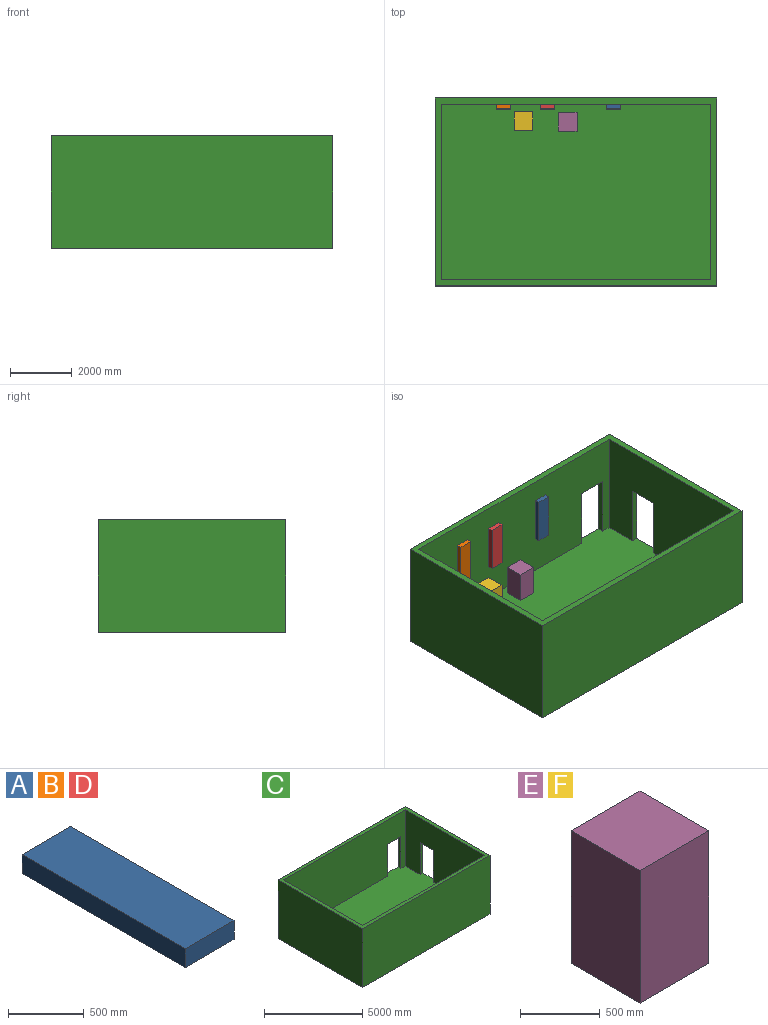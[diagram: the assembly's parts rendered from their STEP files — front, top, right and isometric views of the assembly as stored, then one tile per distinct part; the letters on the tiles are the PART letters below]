
ASSEMBLY  parts=6 mates=5
PART A: 6 faces, bbox 457.2x1524x152.4 mm
  f0: plane 457.2x152.4mm, normal (0,1,0), area 69677.3mm2, adj f1,f3,f4,f5
  f1: plane 1524x152.4mm, normal (-1,0,0), area 232257.6mm2, adj f0,f2,f4,f5
  f2: plane 457.2x152.4mm, normal (0,-1,0), area 69677.3mm2, adj f1,f3,f4,f5
  f3: plane 1524x152.4mm, normal (1,0,0), area 232257.6mm2, adj f0,f2,f4,f5
  f4: plane 1524x457.2mm, normal (0,0,1), area 696772.8mm2, adj f0,f1,f2,f3
  f5: plane 1524x457.2mm, normal (0,0,-1), area 696772.8mm2, adj f0,f1,f2,f3
PART B: same geometry as A
PART C: 17 faces, bbox 9144x6096x3657.6 mm
  f0: plane 1981.2x203.2mm, normal (0,1,0), area 402579.8mm2, adj f4,f5,f10,f16
  f1: plane 1981.2x203.2mm, normal (0,-1,0), area 402579.8mm2, adj f4,f5,f10,f16
  f2: plane 1981.2x203.2mm, normal (1,0,0), area 402579.8mm2, adj f4,f6,f13,f15
  f3: plane 1981.2x203.2mm, normal (-1,0,0), area 402579.8mm2, adj f4,f6,f13,f15
  f4: plane 8940.8x5892.8mm, normal (0,0,1), area 50105706.2mm2, adj f0,f1,f2,f3,f5,f6,f10,f11
  f5: plane 6096x3657.6mm, normal (1,0,0), area 20384475.4mm2, adj f0,f1,f4,f6,f8,f9,f14,f16
  f6: plane 9144x3657.6mm, normal (0,1,0), area 31532840.2mm2, adj f2,f3,f4,f5,f7,f9,f14,f15
  f7: plane 6096x3657.6mm, normal (-1,0,0), area 22296729.6mm2, adj f6,f8,f9,f14
  f8: plane 9144x3657.6mm, normal (0,-1,0), area 33445094.4mm2, adj f5,f7,f9,f14
  f9: plane 9144x6096mm, normal (0,0,-1), area 55741824mm2, adj f5,f6,f7,f8
  f10: plane 5689.6x3505.2mm, normal (-1,0,0), area 18030931.7mm2, adj f0,f1,f4,f11,f13,f14,f16
  f11: plane 8737.6x3505.2mm, normal (0,1,0), area 30627035.5mm2, adj f4,f10,f12,f14
  f12: plane 5689.6x3505.2mm, normal (1,0,0), area 19943185.9mm2, adj f4,f11,f13,f14
  f13: plane 8737.6x3505.2mm, normal (0,-1,0), area 28714781.3mm2, adj f2,f3,f4,f10,f12,f14,f15
  f14: plane 9144x6096mm, normal (0,0,1), area 6028375mm2, adj f5,f6,f7,f8,f10,f11,f12,f13
  f15: plane 965.2x203.2mm, normal (0,0,-1), area 196128.6mm2, adj f2,f3,f6,f13
  f16: plane 965.2x203.2mm, normal (0,0,-1), area 196128.6mm2, adj f0,f1,f5,f10
PART D: same geometry as A
PART E: 6 faces, bbox 609.6x609.6x1016 mm
  f0: plane 1016x609.6mm, normal (0,-1,0), area 619353.6mm2, adj f1,f3,f4,f5
  f1: plane 1016x609.6mm, normal (1,0,0), area 619353.6mm2, adj f0,f2,f4,f5
  f2: plane 1016x609.6mm, normal (0,1,0), area 619353.6mm2, adj f1,f3,f4,f5
  f3: plane 1016x609.6mm, normal (-1,0,0), area 619353.6mm2, adj f0,f2,f4,f5
  f4: plane 609.6x609.6mm, normal (0,0,1), area 371612.2mm2, adj f0,f1,f2,f3
  f5: plane 609.6x609.6mm, normal (0,0,-1), area 371612.2mm2, adj f0,f1,f2,f3
PART F: same geometry as E
PLACE A rot(axis=(1,0,0),90deg) t=(-960.18,3461.84,2115.74)mm
PLACE B rot(axis=(-1,0,0),90deg) t=(-4530.67,3309.44,3647.85)mm
PLACE C t=(-1886.96,-322.76,727.22)mm fixed
PLACE D rot(axis=(1,0,0),90deg) t=(-3097.43,3461.84,2082.88)mm
PLACE E rot(axis=(1,0,0),180deg) t=(-1649.13,3201.16,1895.62)mm
PLACE F rot(axis=(1,0,0),180deg) t=(-3082.52,3223.97,1895.62)mm
MATE planar B.f4 <-> C.f13  axis (0,1,0) through (-4048.07,3461.84,2885.85)mm
MATE planar A.f5 <-> C.f13  axis (0,1,0) through (-477.58,3461.84,2877.74)mm
MATE planar F.f4 <-> C.f4  axis (0,0,-1) through (-3387.32,2919.17,879.62)mm
MATE planar E.f4 <-> C.f4  axis (0,0,-1) through (-1953.93,2896.36,879.62)mm
MATE planar D.f5 <-> C.f13  axis (0,1,0) through (-2614.83,3461.84,2844.88)mm
